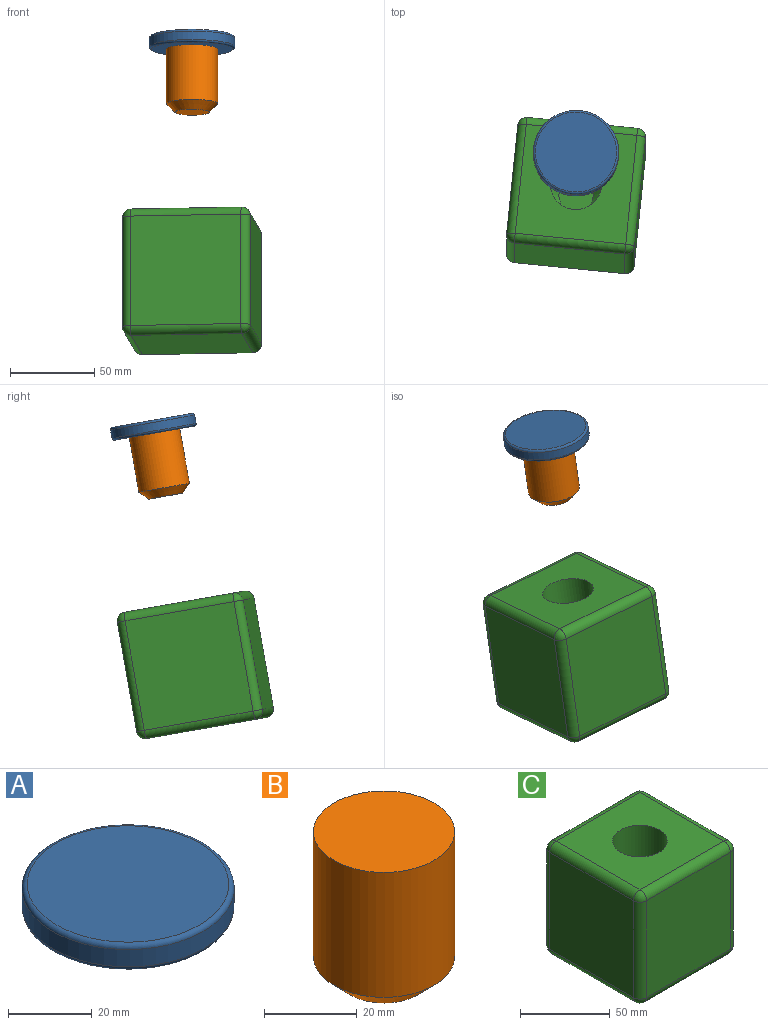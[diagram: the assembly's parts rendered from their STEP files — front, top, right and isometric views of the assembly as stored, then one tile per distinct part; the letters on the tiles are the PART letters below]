
ASSEMBLY  parts=3 mates=2
PART A: 5 faces, bbox 55x55x7.6 mm
  f0: cylinder r=25.4mm len=50.8mm, axis (0,0,-1), area 810.7mm2, adj f3,f4
  f1: plane 48.26x48.26mm, normal (0,0,1), area 1829.2mm2, adj f4
  f2: plane 48.26x48.26mm, normal (0,0,-1), area 1829.2mm2, adj f3
  f3: torus R=24.13mm, axis (0,0,1), area 312.6mm2, adj f0,f2
  f4: torus R=24.13mm, axis (0,0,1), area 312.6mm2, adj f0,f1
PART B: 4 faces, bbox 30.5x30.5x38.1 mm
  f0: cylinder r=15.24mm len=33.02mm, axis (0,0,-1), area 3161.9mm2, adj f1,f3
  f1: plane 30.48x30.48mm, normal (0,0,1), area 729.7mm2, adj f0
  f2: plane 20.32x20.32mm, normal (0,0,-1), area 324.3mm2, adj f3
  f3: cone r=15.24mm half-angle=45deg, axis (0,0,1), area 573.3mm2, adj f0,f2
PART C: 29 faces, bbox 76.2x76.2x76.2 mm
  f0: plane 66.04x66.04mm, normal (0,1,0), area 4361.3mm2, adj f17,f22,f25,f28
  f1: plane 66.04x66.04mm, normal (-1,0,0), area 4361.3mm2, adj f14,f23,f24,f28
  f2: plane 66.04x66.04mm, normal (0,-1,0), area 4361.3mm2, adj f9,f13,f14,f15
  f3: plane 66.04x66.04mm, normal (1,0,0), area 4361.3mm2, adj f9,f12,f16,f17
  f4: plane 66.04x66.04mm, normal (0,0,1), area 3631.6mm2, adj f6,f12,f13,f22,f23
  f5: plane 66.04x66.04mm, normal (0,0,-1), area 4361.3mm2, adj f15,f16,f24,f25
  f6: cylinder r=15.24mm len=33.02mm, axis (0,0,1), area 3161.9mm2, adj f4,f8
  f7: plane 20.32x20.32mm, normal (0,0,1), area 324.3mm2, adj f8
  f8: cone r=10.16mm half-angle=45deg, axis (0,0,1), area 573.3mm2, adj f6,f7
  f9: cylinder r=5.08mm len=66.04mm, axis (0,0,1), area 527mm2, adj f2,f3,f10,f11
  f10: sphere r=5.08mm, area 40.5mm2, adj f9,f12,f13
  f11: sphere r=5.08mm, area 40.5mm2, adj f9,f15,f16
  f12: cylinder r=5.08mm len=66.04mm, axis (0,-1,0), area 527mm2, adj f3,f4,f10,f18
  f13: cylinder r=5.08mm len=66.04mm, axis (-1,0,0), area 527mm2, adj f2,f4,f10,f19
  f14: cylinder r=5.08mm len=66.04mm, axis (0,0,-1), area 527mm2, adj f1,f2,f19,f20
  f15: cylinder r=5.08mm len=66.04mm, axis (1,0,0), area 527mm2, adj f2,f5,f11,f20
  f16: cylinder r=5.08mm len=66.04mm, axis (0,1,0), area 527mm2, adj f3,f5,f11,f21
  f17: cylinder r=5.08mm len=66.04mm, axis (0,0,-1), area 527mm2, adj f0,f3,f18,f21
  f18: sphere r=5.08mm, area 40.5mm2, adj f12,f17,f22
  f19: sphere r=5.08mm, area 40.5mm2, adj f13,f14,f23
  f20: sphere r=5.08mm, area 40.5mm2, adj f14,f15,f24
  f21: sphere r=5.08mm, area 40.5mm2, adj f16,f17,f25
  f22: cylinder r=5.08mm len=66.04mm, axis (1,0,0), area 527mm2, adj f0,f4,f18,f26
  f23: cylinder r=5.08mm len=66.04mm, axis (0,1,0), area 527mm2, adj f1,f4,f19,f26
  f24: cylinder r=5.08mm len=66.04mm, axis (0,-1,0), area 527mm2, adj f1,f5,f20,f27
  f25: cylinder r=5.08mm len=66.04mm, axis (-1,0,0), area 527mm2, adj f0,f5,f21,f27
  f26: sphere r=5.08mm, area 40.5mm2, adj f22,f23,f28
  f27: sphere r=5.08mm, area 40.5mm2, adj f24,f25,f28
  f28: cylinder r=5.08mm len=66.04mm, axis (0,0,1), area 527mm2, adj f0,f1,f26,f27
PLACE A rot(axis=(-0.1,0.09,0.99),81.3deg) t=(103.55,-155.52,339.92)mm
PLACE B rot(axis=(-0.1,0.09,0.99),81.3deg) t=(103.55,-155.52,339.92)mm
PLACE C rot(axis=(-0.08,-0.09,-0.99),96.1deg) t=(56.64,-116.36,190.91)mm
MATE cylindrical C.f6 <-> B.f0  axis (0,0.17,0.98) through (56.64,-109.75,228.43)mm
MATE fastened B.f0 <-> A.f0  axis (0,0.17,0.98) through (56.64,-85.45,366.25)mm
